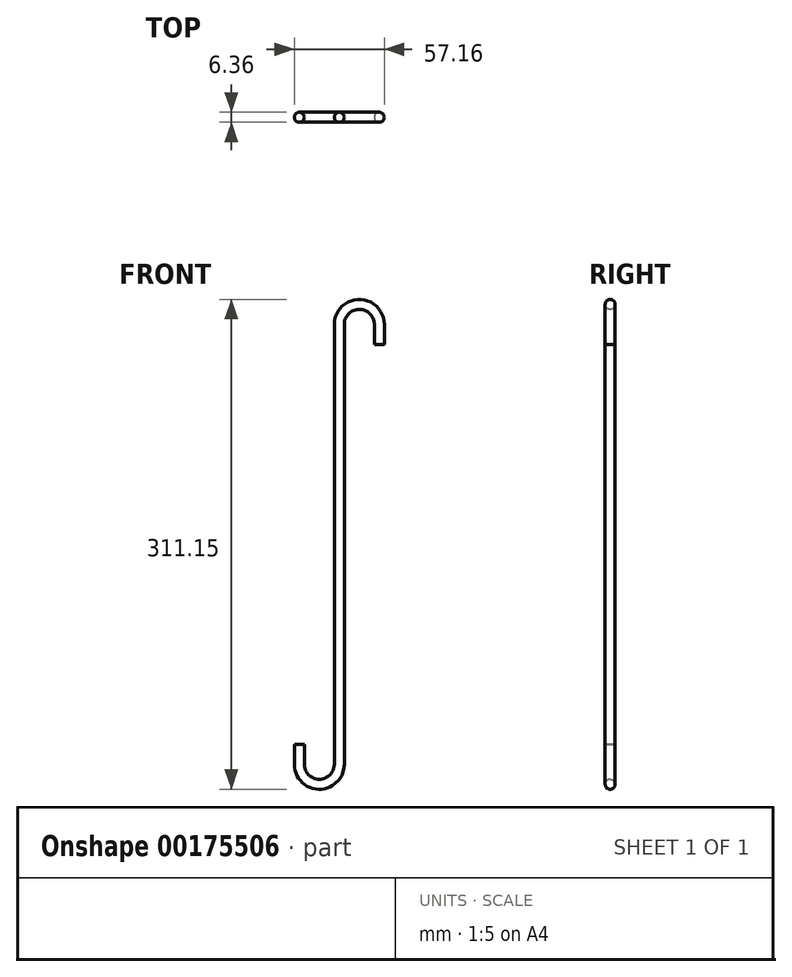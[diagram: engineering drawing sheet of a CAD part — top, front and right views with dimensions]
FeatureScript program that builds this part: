
annotation { "Feature Type Name" : "Feature", "Feature Type Description" : "" }
export const myFeature = defineFeature(function(context is Context, id is Id, definition is map)
    precondition{}
    {
        {
            var Q0;
            Q0=qCreatedBy(makeId("Front.planeOp"),FACE);
            var sketch = newSketch(context, id + "F0", { "sketchPlane" : qUnion([Q0])});
            skLineSegment(sketch, "E0", {"start": v(-50.8, -126.2) * mm, "end": v(-50.8, -138.9) * mm});
            skLineSegment(sketch, "E1", {"start": v(-38.1, -151.6) * mm, "end": v(-38.1, -151.6) * mm});
            skLineSegment(sketch, "E2", {"start": v(-25.4, -138.9) * mm, "end": v(-25.4, 140.5) * mm});
            skLineSegment(sketch, "E3", {"start": v(-12.7, 153.2) * mm, "end": v(-12.7, 153.2) * mm});
            skLineSegment(sketch, "E4", {"start": v(0, 140.5) * mm, "end": v(0, 127.8) * mm});
            skPoint(sketch, "E5.visualSharp", {"position": v(-50.8, -151.6) * mm});
            skArc(sketch, "E5.filletArc", {"start": v(-50.8, -138.9) * mm, "mid": v(-47.08, -147.87) * mm, "end": v(-38.1, -151.6) * mm});
            skPoint(sketch, "E6.visualSharp", {"position": v(-25.4, -151.6) * mm});
            skArc(sketch, "E6.filletArc", {"start": v(-38.1, -151.6) * mm, "mid": v(-29.12, -147.87) * mm, "end": v(-25.4, -138.9) * mm});
            skPoint(sketch, "E7.visualSharp", {"position": v(-25.4, 153.2) * mm});
            skArc(sketch, "E7.filletArc", {"start": v(-12.7, 153.2) * mm, "mid": v(-21.68, 149.49) * mm, "end": v(-25.4, 140.5) * mm});
            skPoint(sketch, "E8.visualSharp", {"position": v(0, 153.2) * mm});
            skArc(sketch, "E8.filletArc", {"start": v(0, 140.5) * mm, "mid": v(-3.72, 149.49) * mm, "end": v(-12.7, 153.2) * mm});
            skSolve(sketch);
        }
        {
            var Q0;
            Q0=sQuery(id+"F0.wireOp",VERTEX,"E0.start");
            var Q1;
            Q1=qCreatedBy(makeId("Top.planeOp"),FACE);
            cPlane(context, id + "F1", {"entities" : qUnion([Q0, Q1]), "cplaneType" : CPlaneType.PLANE_POINT, "offset" : 25.4 * mm, "width" : 152.4 * mm, "height" : 152.4 * mm});
        }
        {
            var Q0;
            Q0=qCreatedBy(id+"F1.planeOp",FACE);
            var sketch = newSketch(context, id + "F2", { "sketchPlane" : qUnion([Q0])});
            skCircle(sketch, "E9", {"center": v(-50.8, 0) * mm, "radius": 3.18 * mm});
            skSolve(sketch);
        }
        {
            var Q0;
            Q0=makeQuery(id+"F2.imprint","IMPRINT",FACE,{"disambiguationData":[TD([[makeQuery(id+"F2.imprint","IMPRINT",EDGE,{"derivedFrom":sQuery(id+"F2.wireOp",EDGE,"E9")}),1.0]])]});
            var Q1;
            Q1=sQuery(id+"F0.wireOp",EDGE,"E0");
            var Q2;
            Q2=sQuery(id+"F0.wireOp",EDGE,"E5.filletArc");
            var Q3;
            Q3=sQuery(id+"F0.wireOp",EDGE,"E6.filletArc");
            var Q4;
            Q4=sQuery(id+"F0.wireOp",EDGE,"E2");
            var Q5;
            Q5=sQuery(id+"F0.wireOp",EDGE,"E7.filletArc");
            var Q6;
            Q6=sQuery(id+"F0.wireOp",EDGE,"E8.filletArc");
            var Q7;
            Q7=sQuery(id+"F0.wireOp",EDGE,"E4");
            sweep(context, id + "F3", {"profiles" : qUnion([Q0]), "path" : qUnion([Q1, Q2, Q3, Q4, Q5, Q6, Q7])});
        }
    });
